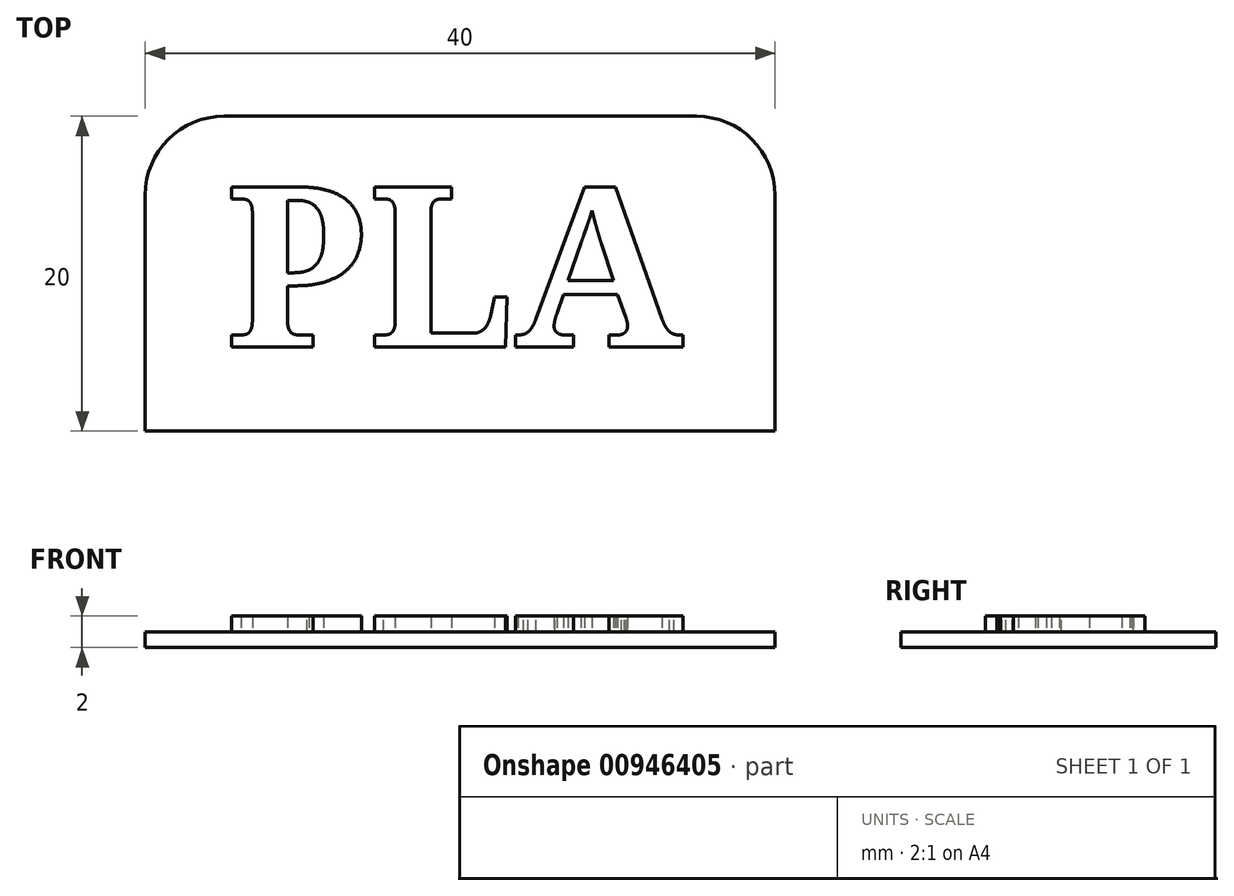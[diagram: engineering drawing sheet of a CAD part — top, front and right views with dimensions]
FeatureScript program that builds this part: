
annotation { "Feature Type Name" : "Feature", "Feature Type Description" : "" }
export const myFeature = defineFeature(function(context is Context, id is Id, definition is map)
    precondition{}
    {
        {
            var Q0;
            Q0=qCreatedBy(makeId("Top.planeOp"),FACE);
            var sketch = newSketch(context, id + "F0", { "sketchPlane" : qUnion([Q0])});
            skLineSegment(sketch, "E0.bottom", {"start": v(-20, 10) * mm, "end": v(20, 10) * mm});
            skLineSegment(sketch, "E0.top", {"start": v(-20, -10) * mm, "end": v(20, -10) * mm});
            skLineSegment(sketch, "E0.left", {"start": v(-20, 10) * mm, "end": v(-20, -10) * mm});
            skLineSegment(sketch, "E0.right", {"start": v(20, 10) * mm, "end": v(20, -10) * mm});
            skPoint(sketch, "E0.middle", {"position": v(0, 0) * mm});
            skSolve(sketch);
        }
        {
            var Q0;
            Q0=makeQuery(id+"F0.imprint","IMPRINT",FACE,{"disambiguationData":[TD([[makeQuery(id+"F0.imprint","IMPRINT",EDGE,{"derivedFrom":sQuery(id+"F0.wireOp",EDGE,"E0.bottom")}),-1.0]])]});
            extrude(context, id + "F1", {"entities" : qUnion([Q0]), "depth" : 1 * mm, "offsetDistance" : 25 * mm});
        }
        {
            var Q0;
            Q0=makeQuery(id+"F1.opExtrude","CAP_FACE",FACE,{"disambiguationData":[OSD([sQuery(id+"F0.wireOp",EDGE,"E0.bottom"),sQuery(id+"F0.wireOp",EDGE,"E0.top"),sQuery(id+"F0.wireOp",EDGE,"E0.left"),sQuery(id+"F0.wireOp",EDGE,"E0.right")])],"isStart":false});
            var sketch = newSketch(context, id + "F2", { "sketchPlane" : qUnion([Q0])});
            skText(sketch, "E1", { "text": "PLA", "fontName": "NotoSerif-Bold.ttf"});
            const initialGuessF2  = {"E1": [-0.01492, -0.00465, 1, 0, 0.01024]};
            skSetInitialGuess(sketch, initialGuessF2);
            skSolve(sketch);
        }
        {
            var Q0;
            Q0 = qSketchRegion(id + "F2", true);
            extrude(context, id + "F3", {"entities" : qUnion([Q0]), "operationType" : NewBodyOperationType.ADD, "depth" : 1 * mm, "offsetDistance" : 25 * mm});
        }
        {
            var Q0;
            Q0=makeQuery(id+"F1.opExtrude","SWEPT_EDGE",EDGE,{"disambiguationData":[OSD([sQuery(id+"F0.wireOp",EDGE,"E0.bottom"),sQuery(id+"F0.wireOp",EDGE,"E0.left")])]});
            var Q1;
            Q1=makeQuery(id+"F1.opExtrude","SWEPT_EDGE",EDGE,{"disambiguationData":[OSD([sQuery(id+"F0.wireOp",EDGE,"E0.bottom"),sQuery(id+"F0.wireOp",EDGE,"E0.right")])]});
            fillet(context, id + "F4", {"entities" : qUnion([Q0, Q1]), "radius" : 5 * mm, "tangentPropagation" : true, "allowEdgeOverflow" : false});
        }
    });
